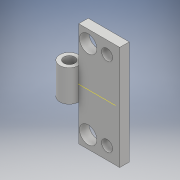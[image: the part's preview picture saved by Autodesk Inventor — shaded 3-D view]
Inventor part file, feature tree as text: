
AUTODESK INVENTOR PART (.ipt)
format: ipt  version: 2017 (Build 210142000, 142)  size: 157,184 bytes
history: native  units: mm
features: extrude x6, sketch x5, plane x1, mirror x1
ambient origin geometry x8: Origin, YZ Plane, XZ Plane, XY Plane, X Axis, Y Axis, Z Axis, Center Point
bodies: Solid1 (feature_tree)
feature tree (13):
  extrude  "Extrusion1"  Depth=33.0mm
  extrude  "Extrusion2"  Depth=3.0mm
  plane  "Work Plane1"
  extrude  "Extrusion3"  Depth=4.0mm
  extrude  "Extrusion4"  Depth=4.0mm
  mirror  "Mirror1"
  extrude  "Extrusion5"  Depth=3.0mm TaperAngle=0.0deg
  extrude  "Extrusion6"  [1 undecoded]
  sketch  "Sketch1"  dims[d3=16.0mm d4=33.0mm]
  sketch  "Sketch2"  dims[d5=3.0mm d6=0.0mm d7=3.5mm]
  sketch  "Sketch4"  dims[d8=3.5mm d9=4.0mm]
  sketch  "Sketch6"  dims[d10=4.0mm d11=4.0mm]
  sketch  "Sketch7"  dims[d12=4.0mm d13=3.0mm d14=0.0mm d16=-16.5mm d17=6.0mm d19=10.0mm d20=0.0mm d22=11.5mm d23=0.0mm d24=3.5mm d25=8.5mm d26=0.0mm d27=5.5mm d28=5.5mm d29=4.0mm d30=4.0mm d31=3.0mm d32=3.0mm d33=10.0mm d34=0.0mm]
note: 1 required parameter value undecoded (feature->parameter linkage not recoverable at this tier; creation-order binding heuristic only, values carry confidence <= 0.55)
